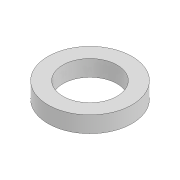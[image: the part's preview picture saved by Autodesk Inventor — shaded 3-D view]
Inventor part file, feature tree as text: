
AUTODESK INVENTOR PART (.ipt)
format: ipt  version: 2022 (Build 260153000, 153)  size: 82,944 bytes
history: native  units: mm
features: extrude x1, sketch x1
ambient origin geometry x8: Origin, YZ Plane, XZ Plane, XY Plane, X Axis, Y Axis, Z Axis, Center Point
bodies: Solid1 (feature_tree)
feature tree (2):
  extrude  "Extrusion1"  Depth=12.0mm
  sketch  "Sketch1"  dims[d0=40.0mm d1=62.0mm d2=12.0mm d3=0.0mm]
